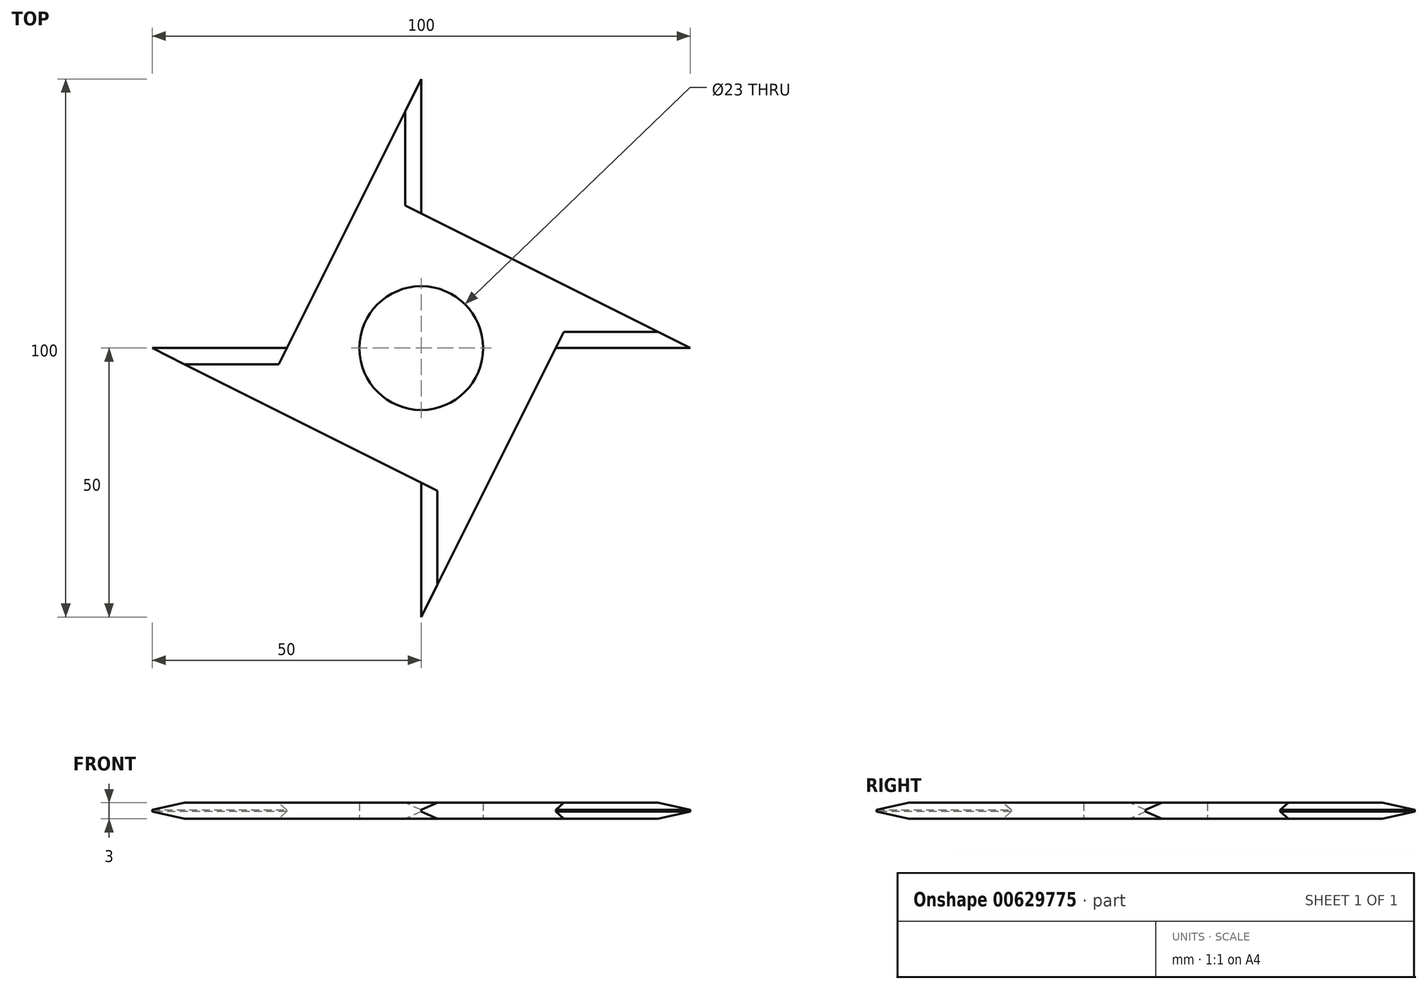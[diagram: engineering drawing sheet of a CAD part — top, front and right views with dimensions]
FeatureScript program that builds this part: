
annotation { "Feature Type Name" : "Feature", "Feature Type Description" : "" }
export const myFeature = defineFeature(function(context is Context, id is Id, definition is map)
    precondition{}
    {
        {
            var Q0;
            Q0=qCreatedBy(makeId("Top.planeOp"),FACE);
            var sketch = newSketch(context, id + "F0", { "sketchPlane" : qUnion([Q0])});
            skCircle(sketch, "E0", {"center": v(0, 0) * mm, "radius": 11.5 * mm});
            skCircle(sketch, "E1", {"center": v(0, 0) * mm, "radius": 25 * mm, "construction": true});
            skLineSegment(sketch, "E2", {"start": v(0, 25) * mm, "end": v(0, 50) * mm});
            skLineSegment(sketch, "E3", {"start": v(0, 50) * mm, "end": v(-25, 0) * mm});
            skLineSegment(sketch, "E4", {"start": v(-25, 0) * mm, "end": v(-50, 0) * mm});
            skLineSegment(sketch, "E5", {"start": v(-50, 0) * mm, "end": v(0, -25) * mm});
            skLineSegment(sketch, "E6", {"start": v(0, -25) * mm, "end": v(0, -50) * mm});
            skLineSegment(sketch, "E7", {"start": v(0, -50) * mm, "end": v(25, 0) * mm});
            skLineSegment(sketch, "E8", {"start": v(25, 0) * mm, "end": v(50, 0) * mm});
            skLineSegment(sketch, "E9", {"start": v(50, 0) * mm, "end": v(0, 25) * mm});
            skCircle(sketch, "E10", {"center": v(0, 0) * mm, "radius": 50 * mm, "construction": true});
            skSolve(sketch);
        }
        {
            var Q0;
            Q0=makeQuery(id+"F0.imprint","IMPRINT",FACE,{"disambiguationData":[TD([[makeQuery(id+"F0.imprint","IMPRINT",EDGE,{"derivedFrom":sQuery(id+"F0.wireOp",EDGE,"E0")}),-1.0]])]});
            extrude(context, id + "F1", {"entities" : qUnion([Q0]), "depth" : 3 * mm, "offsetDistance" : 25 * mm});
        }
        {
            var Q0;
            Q0=makeQuery(id+"F1.opExtrude","CAP_EDGE",EDGE,{"disambiguationData":[OSD([sQuery(id+"F0.wireOp",EDGE,"E2")])],"isStart":false});
            var Q1;
            Q1=makeQuery(id+"F1.opExtrude","CAP_EDGE",EDGE,{"disambiguationData":[OSD([sQuery(id+"F0.wireOp",EDGE,"E8")])],"isStart":false});
            var Q2;
            Q2=makeQuery(id+"F1.opExtrude","CAP_EDGE",EDGE,{"disambiguationData":[OSD([sQuery(id+"F0.wireOp",EDGE,"E6")])],"isStart":false});
            var Q3;
            Q3=makeQuery(id+"F1.opExtrude","CAP_EDGE",EDGE,{"disambiguationData":[OSD([sQuery(id+"F0.wireOp",EDGE,"E4")])],"isStart":false});
            chamfer(context, id + "F2", {"entities" : qUnion([Q0, Q1, Q2, Q3]), "chamferType" : ChamferType.TWO_OFFSETS, "width1" : 3 * mm, "oppositeDirection" : false, "width2" : 1.35 * mm, "tangentPropagation" : true});
        }
        {
            var Q0;
            Q0=makeQuery(id+"F1.opExtrude","CAP_EDGE",EDGE,{"disambiguationData":[OSD([sQuery(id+"F0.wireOp",EDGE,"E8")])],"isStart":true});
            var Q1;
            Q1=makeQuery(id+"F1.opExtrude","CAP_EDGE",EDGE,{"disambiguationData":[OSD([sQuery(id+"F0.wireOp",EDGE,"E2")])],"isStart":true});
            var Q2;
            Q2=makeQuery(id+"F1.opExtrude","CAP_EDGE",EDGE,{"disambiguationData":[OSD([sQuery(id+"F0.wireOp",EDGE,"E4")])],"isStart":true});
            var Q3;
            Q3=makeQuery(id+"F1.opExtrude","CAP_EDGE",EDGE,{"disambiguationData":[OSD([sQuery(id+"F0.wireOp",EDGE,"E6")])],"isStart":true});
            chamfer(context, id + "F3", {"entities" : qUnion([Q0, Q1, Q2, Q3]), "chamferType" : ChamferType.TWO_OFFSETS, "width1" : 1.35 * mm, "oppositeDirection" : false, "width2" : 3 * mm, "tangentPropagation" : true});
        }
    });
